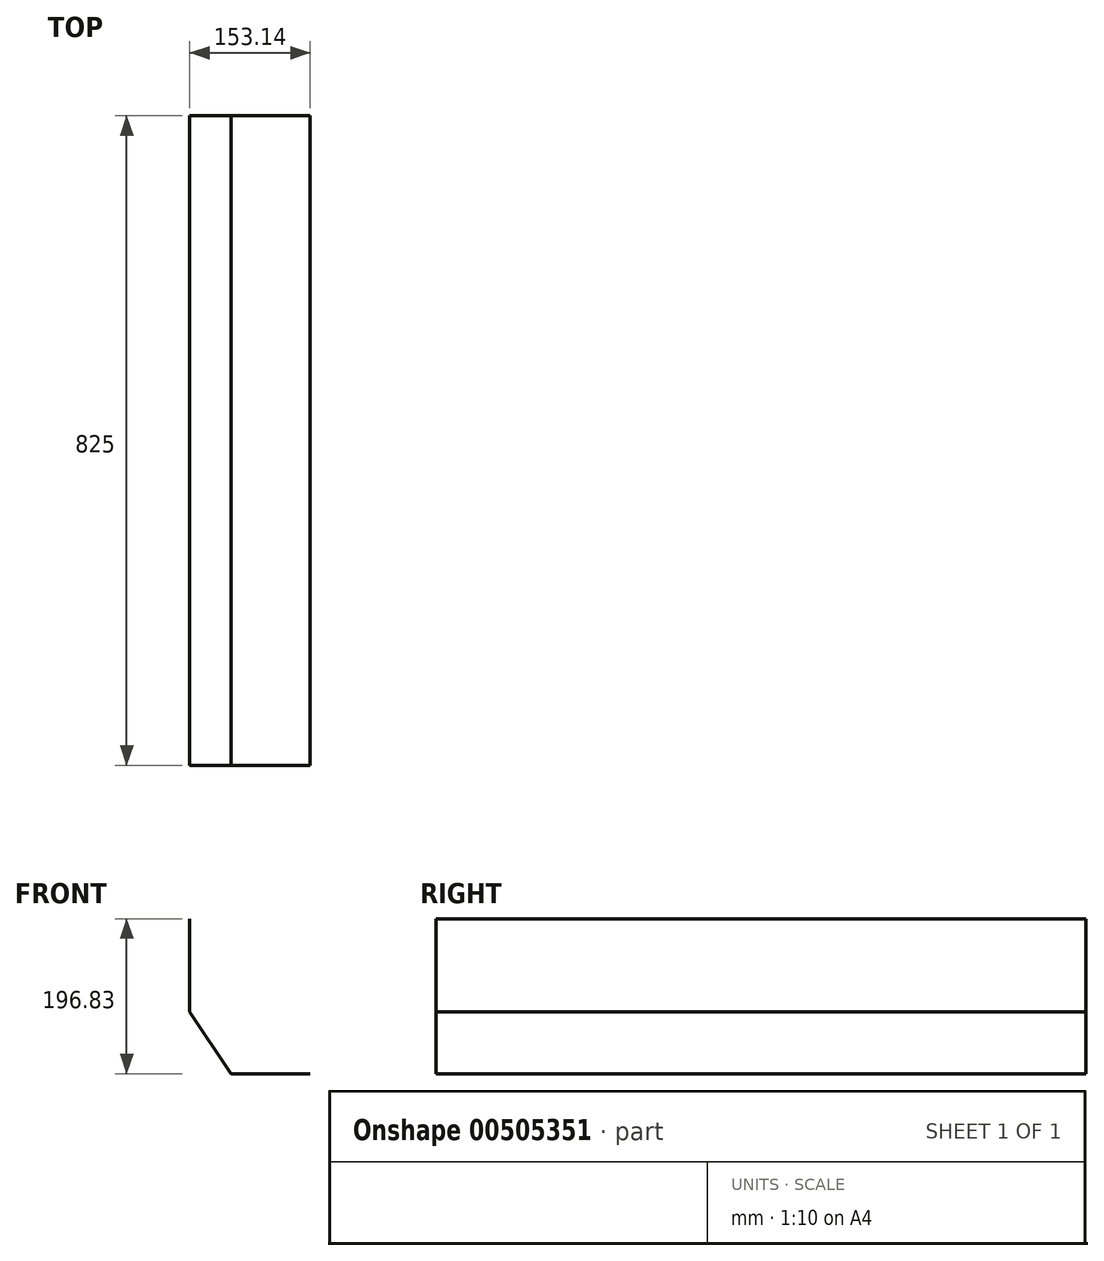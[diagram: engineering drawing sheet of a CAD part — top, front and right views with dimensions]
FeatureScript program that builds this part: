
annotation { "Feature Type Name" : "Feature", "Feature Type Description" : "" }
export const myFeature = defineFeature(function(context is Context, id is Id, definition is map)
    precondition{}
    {
        {
            var Q0;
            Q0=qCreatedBy(makeId("Front.planeOp"),FACE);
            var sketch = newSketch(context, id + "F0", { "sketchPlane" : qUnion([Q0])});
            skLineSegment(sketch, "E0", {"start": v(0, 0) * mm, "end": v(-100.82, 0) * mm});
            skLineSegment(sketch, "E1", {"start": v(-100.82, 0) * mm, "end": v(-153.14, 78.62) * mm});
            skLineSegment(sketch, "E2", {"start": v(-153.14, 78.62) * mm, "end": v(-153.14, 196.83) * mm});
            skSolve(sketch);
        }
        {
            var Q0;
            Q0=sQuery(id+"F0.wireOp",EDGE,"E2");
            var Q1;
            Q1=sQuery(id+"F0.wireOp",EDGE,"E1");
            var Q2;
            Q2=sQuery(id+"F0.wireOp",EDGE,"E0");
            extrude(context, id + "F1", {"bodyType" : ToolBodyType.SURFACE, "surfaceEntities" : qUnion([Q0, Q1, Q2]), "depth" : 825 * mm, "offsetDistance" : 25 * mm});
        }
    });
